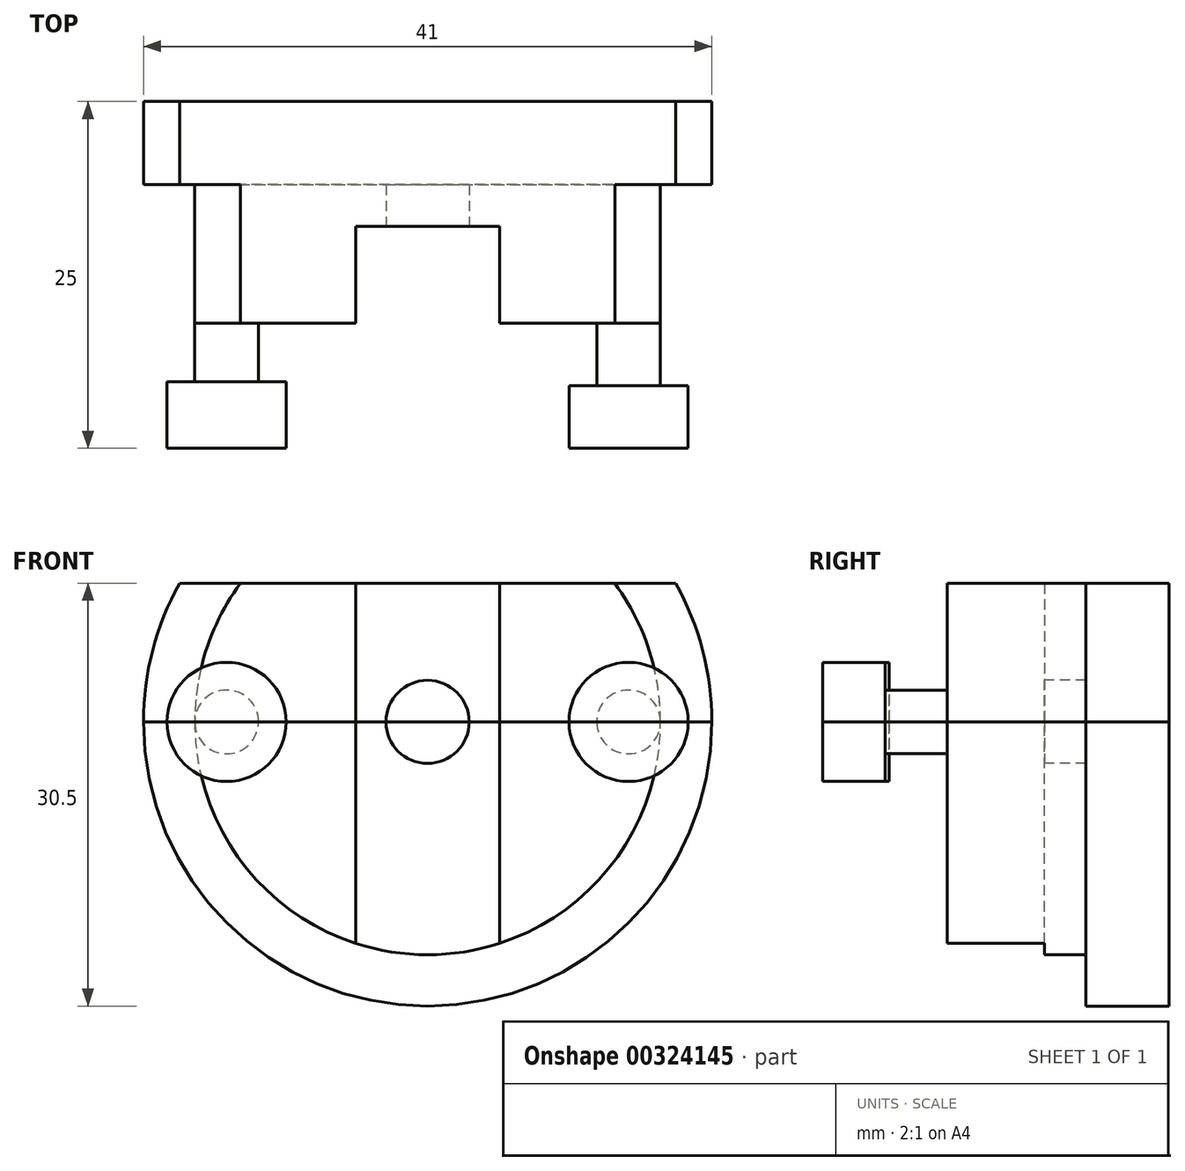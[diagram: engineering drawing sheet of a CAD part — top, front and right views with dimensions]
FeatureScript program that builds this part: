
annotation { "Feature Type Name" : "Feature", "Feature Type Description" : "" }
export const myFeature = defineFeature(function(context is Context, id is Id, definition is map)
    precondition{}
    {
        {
            var Q0;
            Q0=qCreatedBy(makeId("Front.planeOp"),FACE);
            var sketch = newSketch(context, id + "F0", { "sketchPlane" : qUnion([Q0])});
            skCircle(sketch, "E0", {"center": v(0, 0) * mm, "radius": 16.8 * mm});
            skSolve(sketch);
        }
        {
            var Q0;
            Q0=makeQuery(id+"F0.imprint","IMPRINT",FACE,{"disambiguationData":[TD([[makeQuery(id+"F0.imprint","IMPRINT",EDGE,{"derivedFrom":sQuery(id+"F0.wireOp",EDGE,"E0")}),1.0]])]});
            extrude(context, id + "F1", {"entities" : qUnion([Q0]), "depth" : 10 * mm});
        }
        {
            var Q0;
            Q0=qCreatedBy(makeId("Top.planeOp"),FACE);
            var sketch = newSketch(context, id + "F2", { "sketchPlane" : qUnion([Q0])});
            skLineSegment(sketch, "E1", {"start": v(-16.8, -10) * mm, "end": v(-16.8, -14.2) * mm});
            skLineSegment(sketch, "E2", {"start": v(-16.8, -14.2) * mm, "end": v(-18.8, -14.2) * mm});
            skLineSegment(sketch, "E3", {"start": v(-18.8, -14.2) * mm, "end": v(-18.8, -19) * mm});
            skLineSegment(sketch, "E4", {"start": v(-18.8, -19) * mm, "end": v(-14.5, -19) * mm});
            skLineSegment(sketch, "E5", {"start": v(-14.5, -19) * mm, "end": v(-14.5, -10) * mm});
            skLineSegment(sketch, "E6", {"start": v(-14.5, -10) * mm, "end": v(-16.8, -10) * mm});
            skLineSegment(sketch, "E7", {"start": v(14.5, -10) * mm, "end": v(14.5, -19) * mm});
            skLineSegment(sketch, "E8", {"start": v(14.5, -19) * mm, "end": v(18.8, -19) * mm});
            skLineSegment(sketch, "E9", {"start": v(18.8, -19) * mm, "end": v(18.8, -14.5) * mm});
            skLineSegment(sketch, "E10", {"start": v(18.8, -14.5) * mm, "end": v(16.8, -14.5) * mm});
            skLineSegment(sketch, "E11", {"start": v(16.8, -14.5) * mm, "end": v(16.8, -10) * mm});
            skLineSegment(sketch, "E12", {"start": v(16.8, -10) * mm, "end": v(14.5, -10) * mm});
            skSolve(sketch);
        }
        {
            var Q0;
            Q0=makeQuery(id+"F2.imprint","IMPRINT",FACE,{"disambiguationData":[TD([[makeQuery(id+"F2.imprint","IMPRINT",EDGE,{"derivedFrom":sQuery(id+"F2.wireOp",EDGE,"E1")}),1.0]])]});
            var Q1;
            Q1=sQuery(id+"F2.wireOp",EDGE,"E5");
            revolve(context, id + "F3", {"operationType" : NewBodyOperationType.ADD, "entities" : qUnion([Q0]), "axis" : qUnion([Q1]), "revolveType" : RevolveType.FULL});
        }
        {
            var Q0;
            Q0=makeQuery(id+"F2.imprint","IMPRINT",FACE,{"disambiguationData":[TD([[makeQuery(id+"F2.imprint","IMPRINT",EDGE,{"derivedFrom":sQuery(id+"F2.wireOp",EDGE,"E7")}),1.0]])]});
            var Q1;
            Q1=sQuery(id+"F2.wireOp",EDGE,"E7");
            revolve(context, id + "F4", {"operationType" : NewBodyOperationType.ADD, "entities" : qUnion([Q0]), "axis" : qUnion([Q1]), "revolveType" : RevolveType.FULL});
        }
        {
            var Q0;
            Q0=qCreatedBy(makeId("Top.planeOp"),FACE);
            var sketch = newSketch(context, id + "F5", { "sketchPlane" : qUnion([Q0])});
            skLineSegment(sketch, "E13.bottom", {"start": v(-31.93, -26.66) * mm, "end": v(31.93, -26.66) * mm});
            skLineSegment(sketch, "E13.top", {"start": v(-31.93, 26.66) * mm, "end": v(31.93, 26.66) * mm});
            skLineSegment(sketch, "E13.left", {"start": v(-31.93, -26.66) * mm, "end": v(-31.93, 26.66) * mm});
            skLineSegment(sketch, "E13.right", {"start": v(31.93, -26.66) * mm, "end": v(31.93, 26.66) * mm});
            skPoint(sketch, "E13.middle", {"position": v(0, 0) * mm});
            skSolve(sketch);
        }
        {
            var Q0;
            Q0=qSketchRegion(id+"F5",true);
            extrude(context, id + "F6", {"entities" : qUnion([Q0]), "operationType" : NewBodyOperationType.REMOVE, "oppositeDirection" : true, "depth" : 25 * mm});
        }
        {
            var Q0;
            Q0=makeQuery(id+"F1.opExtrude","SWEPT_BODY",BODY,{"disambiguationData":[OSD([sQuery(id+"F0.wireOp",EDGE,"E0"),sQuery(id+"F0.wireOp",EDGE,"sVUXzrZq-DFpS-s5g5-4qUc-trCpaDZMh907.bottom"),sQuery(id+"F0.wireOp",EDGE,"sVUXzrZq-DFpS-s5g5-4qUc-trCpaDZMh907.top"),sQuery(id+"F0.wireOp",EDGE,"sVUXzrZq-DFpS-s5g5-4qUc-trCpaDZMh907.left"),sQuery(id+"F0.wireOp",EDGE,"sVUXzrZq-DFpS-s5g5-4qUc-trCpaDZMh907.right")])]});
            var Q1;
            Q1=qCreatedBy(makeId("Top.planeOp"),FACE);
            mirror(context, id + "F7", {"entities" : qUnion([Q0]), "mirrorPlane" : qUnion([Q1])});
        }
        {
            var Q0;
            Q0=makeQuery(id+"F1.opExtrude","CAP_FACE",FACE,{"disambiguationData":[OSD([sQuery(id+"F0.wireOp",EDGE,"E0"),sQuery(id+"F0.wireOp",EDGE,"sVUXzrZq-DFpS-s5g5-4qUc-trCpaDZMh907.bottom"),sQuery(id+"F0.wireOp",EDGE,"sVUXzrZq-DFpS-s5g5-4qUc-trCpaDZMh907.top"),sQuery(id+"F0.wireOp",EDGE,"sVUXzrZq-DFpS-s5g5-4qUc-trCpaDZMh907.left"),sQuery(id+"F0.wireOp",EDGE,"sVUXzrZq-DFpS-s5g5-4qUc-trCpaDZMh907.right")])],"isStart":false});
            var sketch = newSketch(context, id + "F8", { "sketchPlane" : qUnion([Q0])});
            skLineSegment(sketch, "E14.bottom", {"start": v(-5.2, 25.87) * mm, "end": v(5.2, 25.87) * mm});
            skLineSegment(sketch, "E14.top", {"start": v(-5.2, -25.87) * mm, "end": v(5.2, -25.87) * mm});
            skLineSegment(sketch, "E14.left", {"start": v(-5.2, 25.87) * mm, "end": v(-5.2, -25.87) * mm});
            skLineSegment(sketch, "E14.right", {"start": v(5.2, 25.87) * mm, "end": v(5.2, -25.87) * mm});
            skPoint(sketch, "E14.middle", {"position": v(0, 0) * mm});
            skSolve(sketch);
        }
        {
            var Q0;
            {var subQ1=sQuery(id+"F0.wireOp",EDGE,"sVUXzrZq-DFpS-s5g5-4qUc-trCpaDZMh907.left");var subQ17=makeQuery(id+"F1.opExtrude","CAP_EDGE",EDGE,{"disambiguationData":[OSD([subQ1])],"isStart":false});Q0=makeQuery(id+"F8.imprint","IMPRINT",FACE,{"disambiguationData":[TD([[makeQuery(id+"F8.imprint","IMPRINT",EDGE,{"derivedFrom":subQ17}),-1.0]])]});}
            var Q1;
            {var subQ5=sQuery(id+"F8.wireOp",EDGE,"E14.top");Q1=makeQuery(id+"F8.imprint","IMPRINT",FACE,{"disambiguationData":[TD([[makeQuery(id+"F8.imprint","IMPRINT",EDGE,{"derivedFrom":subQ5}),1.0]])]});}
            var Q2;
            {var subQ0=sQuery(id+"F8.wireOp",EDGE,"E14.left");var subQ1=sQuery(id+"F0.wireOp",EDGE,"E0");var subQ2=makeQuery(id+"F4.boolean.opBoolean","SPLIT",EDGE,{"disambiguationData":[OD(1.0)],"derivedFrom":makeQuery(id+"F1.opExtrude","CAP_EDGE",EDGE,{"disambiguationData":[OSD([subQ1])],"isStart":false})});var subQ3=makeQuery(id+"F8.imprint","INTERSECT",VERTEX,{"derivedFrom":[subQ2,subQ0]});Q2=makeQuery(id+"F8.imprint","IMPRINT",FACE,{"disambiguationData":[TD([[makeQuery(id+"F8.imprint","IMPRINT",EDGE,{"disambiguationData":[TD([[subQ3,1.0]])],"derivedFrom":subQ2}),1.0]])]});}
            extrude(context, id + "F9", {"entities" : qUnion([Q0, Q1, Q2]), "operationType" : NewBodyOperationType.REMOVE, "oppositeDirection" : true, "depth" : 7 * mm});
        }
        {
            var Q0;
            {var subQ0=sQuery(id+"F0.wireOp",EDGE,"E0");var subQ1=sQuery(id+"F8.wireOp",EDGE,"E14.left");var subQ2=sQuery(id+"F8.wireOp",EDGE,"E14.right");Q0=makeQuery(id+"F9.boolean.opBoolean","COPY",FACE,{"disambiguationData":[TD([makeQuery(id+"F1.opExtrude","SWEPT_FACE",FACE,{"disambiguationData":[OSD([subQ0])]})])],"derivedFrom":makeQuery(id+"F9.opExtrude","CAP_FACE",FACE,{"disambiguationData":[OSD([subQ0,sQuery(id+"F8.wireOp",EDGE,"E14.top"),subQ1,subQ2])],"isStart":false})});}
            var sketch = newSketch(context, id + "F10", { "sketchPlane" : qUnion([Q0])});
            skCircle(sketch, "E15", {"center": v(0, 0) * mm, "radius": 3 * mm});
            skSolve(sketch);
        }
        {
            var Q0;
            {var subQ0=sQuery(id+"F10.wireOp",EDGE,"E15");var subQ1=makeQuery(id+"F9.boolean.opBoolean","INTERSECT",EDGE,{"derivedFrom":[makeQuery(id+"F6.boolean.opBoolean","COPY",FACE,{"derivedFrom":makeQuery(id+"F6.opExtrude","CAP_FACE",FACE,{"disambiguationData":[OSD([sQuery(id+"F5.wireOp",EDGE,"E13.bottom"),sQuery(id+"F5.wireOp",EDGE,"E13.top"),sQuery(id+"F5.wireOp",EDGE,"E13.left"),sQuery(id+"F5.wireOp",EDGE,"E13.right")])],"isStart":true})}),makeQuery(id+"F9.opExtrude","CAP_FACE",FACE,{"disambiguationData":[OSD([sQuery(id+"F0.wireOp",EDGE,"E0"),sQuery(id+"F8.wireOp",EDGE,"E14.top"),sQuery(id+"F8.wireOp",EDGE,"E14.left"),sQuery(id+"F8.wireOp",EDGE,"E14.right")])],"isStart":false})]});var subQ2=makeQuery(id+"F10.imprint","INTERSECT",VERTEX,{"disambiguationData":[OD(0.0)],"derivedFrom":[subQ1,subQ0]});Q0=makeQuery(id+"F10.imprint","IMPRINT",FACE,{"disambiguationData":[TD([[makeQuery(id+"F10.imprint","IMPRINT",EDGE,{"disambiguationData":[TD([[subQ2,1.0]])],"derivedFrom":subQ0}),1.0]])]});}
            var Q1;
            {var subQ0=sQuery(id+"F10.wireOp",EDGE,"E15");var subQ1=makeQuery(id+"F9.boolean.opBoolean","INTERSECT",EDGE,{"derivedFrom":[makeQuery(id+"F6.boolean.opBoolean","COPY",FACE,{"derivedFrom":makeQuery(id+"F6.opExtrude","CAP_FACE",FACE,{"disambiguationData":[OSD([sQuery(id+"F5.wireOp",EDGE,"E13.bottom"),sQuery(id+"F5.wireOp",EDGE,"E13.top"),sQuery(id+"F5.wireOp",EDGE,"E13.left"),sQuery(id+"F5.wireOp",EDGE,"E13.right")])],"isStart":true})}),makeQuery(id+"F9.opExtrude","CAP_FACE",FACE,{"disambiguationData":[OSD([sQuery(id+"F0.wireOp",EDGE,"E0"),sQuery(id+"F8.wireOp",EDGE,"E14.top"),sQuery(id+"F8.wireOp",EDGE,"E14.left"),sQuery(id+"F8.wireOp",EDGE,"E14.right")])],"isStart":false})]});var subQ2=makeQuery(id+"F10.imprint","INTERSECT",VERTEX,{"disambiguationData":[OD(0.0)],"derivedFrom":[subQ1,subQ0]});Q1=makeQuery(id+"F10.imprint","IMPRINT",FACE,{"disambiguationData":[TD([[makeQuery(id+"F10.imprint","IMPRINT",EDGE,{"disambiguationData":[TD([[subQ2,-1.0]])],"derivedFrom":subQ0}),1.0]])]});}
            extrude(context, id + "F11", {"entities" : qUnion([Q0, Q1]), "operationType" : NewBodyOperationType.REMOVE, "oppositeDirection" : true, "depth" : 25 * mm});
        }
        {
            var Q0;
            Q0=makeQuery(id+"F1.opExtrude","CAP_FACE",FACE,{"disambiguationData":[OSD([sQuery(id+"F0.wireOp",EDGE,"E0")])],"isStart":true});
            var sketch = newSketch(context, id + "F12", { "sketchPlane" : qUnion([Q0])});
            skCircle(sketch, "E16", {"center": v(0, 0) * mm, "radius": 20.5 * mm});
            skSolve(sketch);
        }
        {
            var Q0;
            {var subQ0=sQuery(id+"F0.wireOp",EDGE,"E0");Q0=makeQuery(id+"F12.imprint","IMPRINT",FACE,{"disambiguationData":[TD([[makeQuery(id+"F12.imprint","IMPRINT",EDGE,{"derivedFrom":makeQuery(id+"F1.opExtrude","CAP_EDGE",EDGE,{"disambiguationData":[OSD([subQ0])],"isStart":true})}),-1.0]])]});}
            var Q1;
            Q1=makeQuery(id+"F12.imprint","IMPRINT",FACE,{"disambiguationData":[TD([[makeQuery(id+"F12.imprint","IMPRINT",EDGE,{"derivedFrom":sQuery(id+"F12.wireOp",EDGE,"E16")}),1.0]])]});
            extrude(context, id + "F13", {"entities" : qUnion([Q0, Q1]), "operationType" : NewBodyOperationType.ADD, "depth" : 6 * mm});
        }
        {
            var Q0;
            Q0=makeQuery(id+"F9.boolean.opBoolean","INTERSECT",EDGE,{"derivedFrom":[makeQuery(id+"F7.opPattern","COPY",FACE,{"derivedFrom":makeQuery(id+"F1.opExtrude","SWEPT_FACE",FACE,{"disambiguationData":[OSD([sQuery(id+"F0.wireOp",EDGE,"E0")])]}),"instanceName":"1"}),makeQuery(id+"F9.opExtrude","SWEPT_FACE",FACE,{"disambiguationData":[OSD([sQuery(id+"F8.wireOp",EDGE,"E14.right")])]})]});
            var Q1;
            Q1=makeQuery(id+"F9.boolean.opBoolean","INTERSECT",EDGE,{"derivedFrom":[makeQuery(id+"F7.opPattern","COPY",FACE,{"derivedFrom":makeQuery(id+"F1.opExtrude","SWEPT_FACE",FACE,{"disambiguationData":[OSD([sQuery(id+"F0.wireOp",EDGE,"E0")])]}),"instanceName":"1"}),makeQuery(id+"F9.opExtrude","SWEPT_FACE",FACE,{"disambiguationData":[OSD([sQuery(id+"F8.wireOp",EDGE,"E14.left")])]})]});
            var Q2;
            Q2=makeQuery(id+"F9.boolean.opBoolean","COPY",EDGE,{"derivedFrom":makeQuery(id+"F9.opExtrude","SWEPT_EDGE",EDGE,{"disambiguationData":[OSD([sQuery(id+"F0.wireOp",EDGE,"E0"),sQuery(id+"F8.wireOp",EDGE,"E14.right")])]})});
            var Q3;
            Q3=makeQuery(id+"F9.boolean.opBoolean","COPY",EDGE,{"derivedFrom":makeQuery(id+"F9.opExtrude","SWEPT_EDGE",EDGE,{"disambiguationData":[OSD([sQuery(id+"F0.wireOp",EDGE,"E0"),sQuery(id+"F8.wireOp",EDGE,"E14.left")])]})});
            fillet(context, id + "F14", {"entities" : qUnion([Q0, Q1, Q2, Q3]), "radius" : 3 * mm, "tangentPropagation" : true, "allowEdgeOverflow" : false});
        }
        {
            var Q0;
            Q0=qCreatedBy(makeId("Top.planeOp"),FACE);
            var sketch = newSketch(context, id + "F15", { "sketchPlane" : qUnion([Q0])});
            skLineSegment(sketch, "E17.bottom", {"start": v(-26.9, 12.42) * mm, "end": v(26.9, 12.42) * mm});
            skLineSegment(sketch, "E17.top", {"start": v(-26.9, -49.35) * mm, "end": v(26.9, -49.35) * mm});
            skLineSegment(sketch, "E17.left", {"start": v(-26.9, 12.42) * mm, "end": v(-26.9, -49.35) * mm});
            skLineSegment(sketch, "E17.right", {"start": v(26.9, 12.42) * mm, "end": v(26.9, -49.35) * mm});
            skPoint(sketch, "E17.middle", {"position": v(0, -18.46) * mm});
            skSolve(sketch);
        }
        {
            var Q0;
            Q0=makeQuery(id+"F15.imprint","IMPRINT",FACE,{"disambiguationData":[TD([[makeQuery(id+"F15.imprint","IMPRINT",EDGE,{"derivedFrom":sQuery(id+"F15.wireOp",EDGE,"E17.bottom")}),-1.0]])]});
            extrude(context, id + "F16", {"entities" : qUnion([Q0]), "operationType" : NewBodyOperationType.REMOVE, "oppositeDirection" : true, "depth" : 25 * mm});
        }
        {
            var Q0;
            Q0=makeQuery(id+"F1.opExtrude","SWEPT_BODY",BODY,{"disambiguationData":[OSD([sQuery(id+"F0.wireOp",EDGE,"E0")])]});
            var Q1;
            Q1=qCreatedBy(makeId("Top.planeOp"),FACE);
            mirror(context, id + "F17", {"entities" : qUnion([Q0]), "mirrorPlane" : qUnion([Q1])});
        }
        {
            var Q0;
            Q0=qCreatedBy(makeId("Front.planeOp"),FACE);
            var sketch = newSketch(context, id + "F18", { "sketchPlane" : qUnion([Q0])});
            skLineSegment(sketch, "E18.bottom", {"start": v(39.77, 41.47) * mm, "end": v(-33.13, 41.47) * mm});
            skLineSegment(sketch, "E18.top", {"start": v(39.77, 10) * mm, "end": v(-33.13, 10) * mm});
            skLineSegment(sketch, "E18.left", {"start": v(39.77, 41.47) * mm, "end": v(39.77, 10) * mm});
            skLineSegment(sketch, "E18.right", {"start": v(-33.13, 41.47) * mm, "end": v(-33.13, 10) * mm});
            skSolve(sketch);
        }
        {
            var Q0;
            Q0=makeQuery(id+"F18.imprint","IMPRINT",FACE,{"disambiguationData":[TD([[makeQuery(id+"F18.imprint","IMPRINT",EDGE,{"derivedFrom":sQuery(id+"F18.wireOp",EDGE,"E18.bottom")}),1.0]])]});
            extrude(context, id + "F19", {"entities" : qUnion([Q0]), "operationType" : NewBodyOperationType.REMOVE, "oppositeDirection" : true, "depth" : 25 * mm, "hasSecondDirection" : true, "secondDirectionOppositeDirection" : false, "secondDirectionDepth" : 25 * mm});
        }
    });
